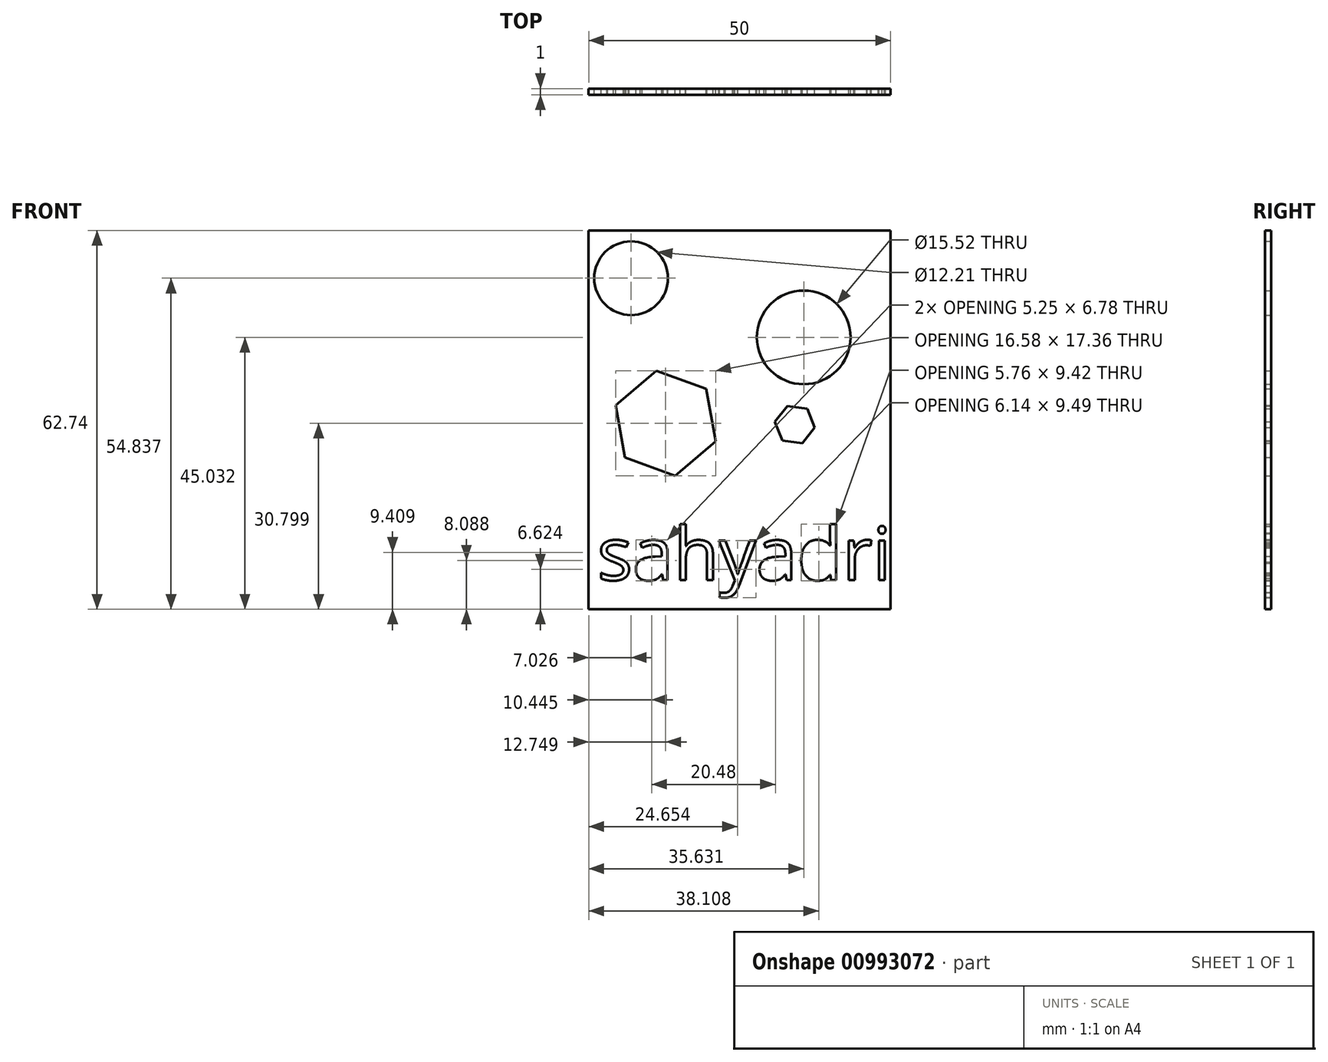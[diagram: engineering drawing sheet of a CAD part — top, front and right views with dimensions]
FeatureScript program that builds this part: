
annotation { "Feature Type Name" : "Feature", "Feature Type Description" : "" }
export const myFeature = defineFeature(function(context is Context, id is Id, definition is map)
    precondition{}
    {
        {
            var Q0;
            Q0=qCreatedBy(makeId("Front.planeOp"),FACE);
            var sketch = newSketch(context, id + "F0", { "sketchPlane" : qUnion([Q0])});
            skLineSegment(sketch, "E0.bottom", {"start": v(-30.72, 35.26) * mm, "end": v(19.28, 35.26) * mm});
            skLineSegment(sketch, "E0.top", {"start": v(-30.72, -27.48) * mm, "end": v(19.28, -27.48) * mm});
            skLineSegment(sketch, "E0.left", {"start": v(-30.72, 35.26) * mm, "end": v(-30.72, -27.48) * mm});
            skLineSegment(sketch, "E0.right", {"start": v(19.28, 35.26) * mm, "end": v(19.28, -27.48) * mm});
            skCircle(sketch, "E1", {"center": v(-23.7, 27.36) * mm, "radius": 6.1 * mm});
            skCircle(sketch, "E2", {"center": v(4.91, 17.55) * mm, "radius": 7.76 * mm});
            skPoint(sketch, "E2.first.point", {"position": v(-2.17, 20.72) * mm});
            skPoint(sketch, "E2.second.point", {"position": v(4, 9.84) * mm});
            skPoint(sketch, "E2.third.point", {"position": v(2.98, 25.07) * mm});
            skCircle(sketch, "E3.cCircle", {"center": v(-17.97, 3.32) * mm, "radius": 7.64 * mm, "construction": true});
            skLineSegment(sketch, "E3.0", {"start": v(-9.68, 0.32) * mm, "end": v(-16.42, -5.36) * mm});
            skLineSegment(sketch, "E3.1", {"start": v(-16.42, -5.36) * mm, "end": v(-24.71, -2.36) * mm});
            skLineSegment(sketch, "E3.2", {"start": v(-24.71, -2.36) * mm, "end": v(-26.26, 6.32) * mm});
            skLineSegment(sketch, "E3.3", {"start": v(-26.26, 6.32) * mm, "end": v(-19.52, 12) * mm});
            skLineSegment(sketch, "E3.4", {"start": v(-19.52, 12) * mm, "end": v(-11.23, 9) * mm});
            skLineSegment(sketch, "E3.5", {"start": v(-11.23, 9) * mm, "end": v(-9.68, 0.32) * mm});
            skPoint(sketch, "E3.0.midPoint", {"position": v(-13.05, -2.52) * mm});
            skCircle(sketch, "E4.cCircle", {"center": v(3.43, 3.1) * mm, "radius": 3.34 * mm, "construction": true});
            skLineSegment(sketch, "E4.0", {"start": v(4.7, 0) * mm, "end": v(1.39, 0.45) * mm});
            skLineSegment(sketch, "E4.1", {"start": v(1.39, 0.45) * mm, "end": v(0.13, 3.55) * mm});
            skLineSegment(sketch, "E4.2", {"start": v(0.13, 3.55) * mm, "end": v(2.17, 6.18) * mm});
            skLineSegment(sketch, "E4.3", {"start": v(2.17, 6.18) * mm, "end": v(5.48, 5.73) * mm});
            skLineSegment(sketch, "E4.4", {"start": v(5.48, 5.73) * mm, "end": v(6.74, 2.64) * mm});
            skLineSegment(sketch, "E4.5", {"start": v(6.74, 2.64) * mm, "end": v(4.7, 0) * mm});
            skText(sketch, "E5", { "text": "sahyadri", "fontName": "OpenSans-Regular.ttf"});
            const initialGuessF0  = {"E5": [-0.0293, -0.02266, 1, 0, 0.00881]};
            skSetInitialGuess(sketch, initialGuessF0);
            skSolve(sketch);
        }
        {
            var Q0;
            Q0 = qSketchRegion(id + "F0", true);
            extrude(context, id + "F1", {"entities" : qUnion([Q0]), "endBound" : BoundingType.SYMMETRIC, "depth" : 1 * mm, "offsetDistance" : 25 * mm});
        }
    });
